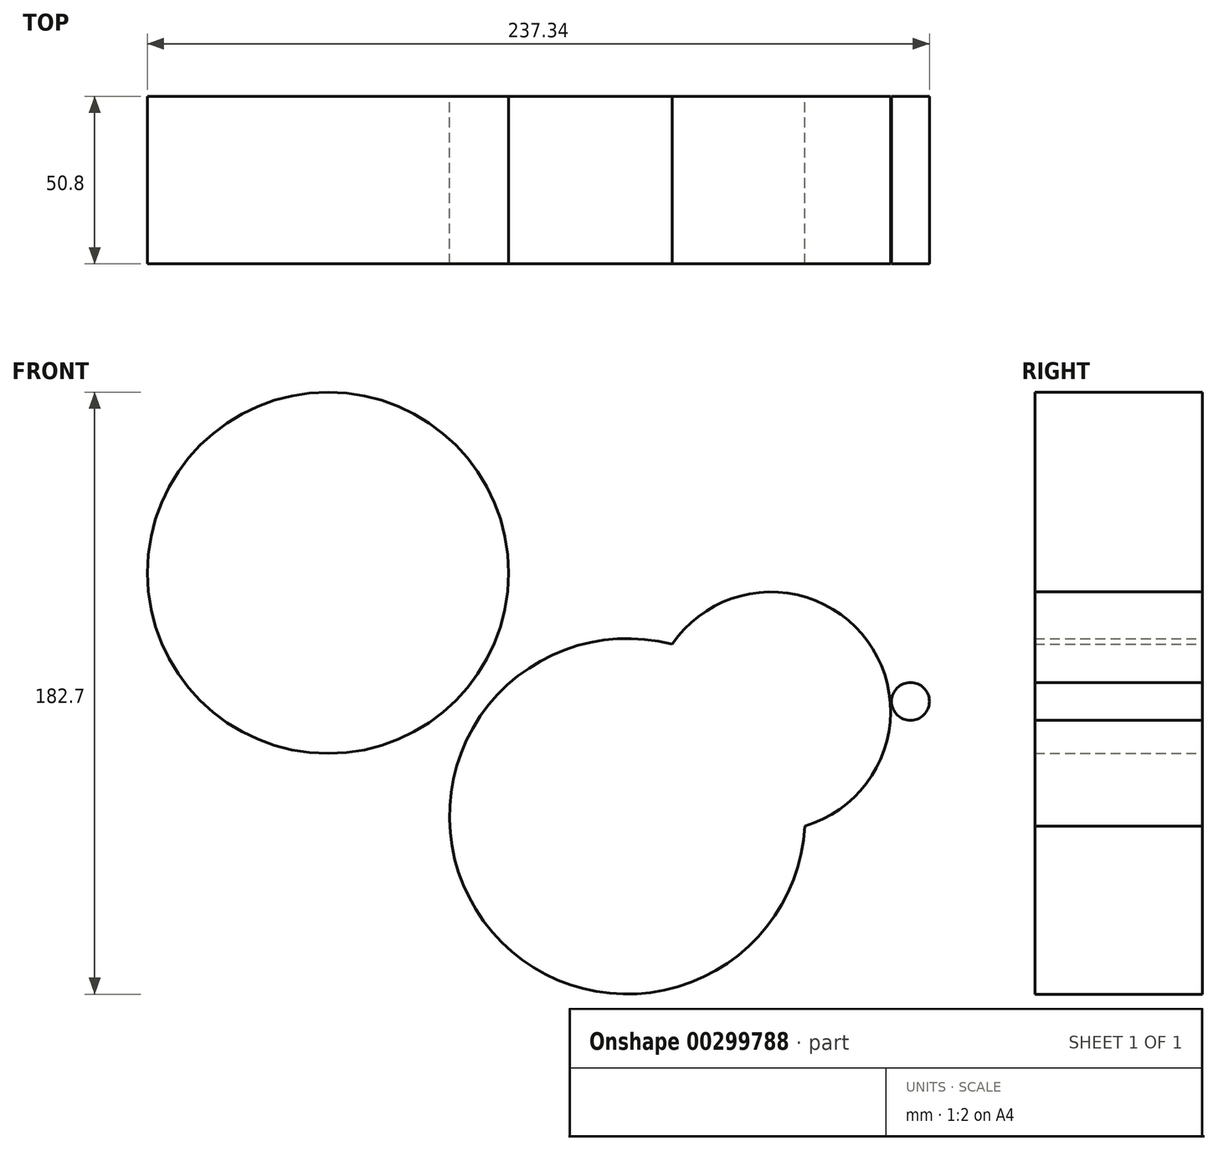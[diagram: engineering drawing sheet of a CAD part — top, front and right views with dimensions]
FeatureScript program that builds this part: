
annotation { "Feature Type Name" : "Feature", "Feature Type Description" : "" }
export const myFeature = defineFeature(function(context is Context, id is Id, definition is map)
    precondition{}
    {
        {
            var Q0;
            Q0=qCreatedBy(makeId("Front.planeOp"),FACE);
            var sketch = newSketch(context, id + "F0", { "sketchPlane" : qUnion([Q0])});
            skCircle(sketch, "E0", {"center": v(0, 0) * mm, "radius": 53.98 * mm});
            skCircle(sketch, "E1", {"center": v(43.6, 31.81) * mm, "radius": 36.28 * mm});
            skCircle(sketch, "E2", {"center": v(85.94, 34.88) * mm, "radius": 5.75 * mm});
            skCircle(sketch, "E3", {"center": v(-90.83, 73.9) * mm, "radius": 54.82 * mm});
            skSolve(sketch);
        }
        {
            var Q0;
            Q0 = qSketchRegion(id + "F0", true);
            extrude(context, id + "F1", {"entities" : qUnion([Q0]), "depth" : 50.8 * mm});
        }
    });
